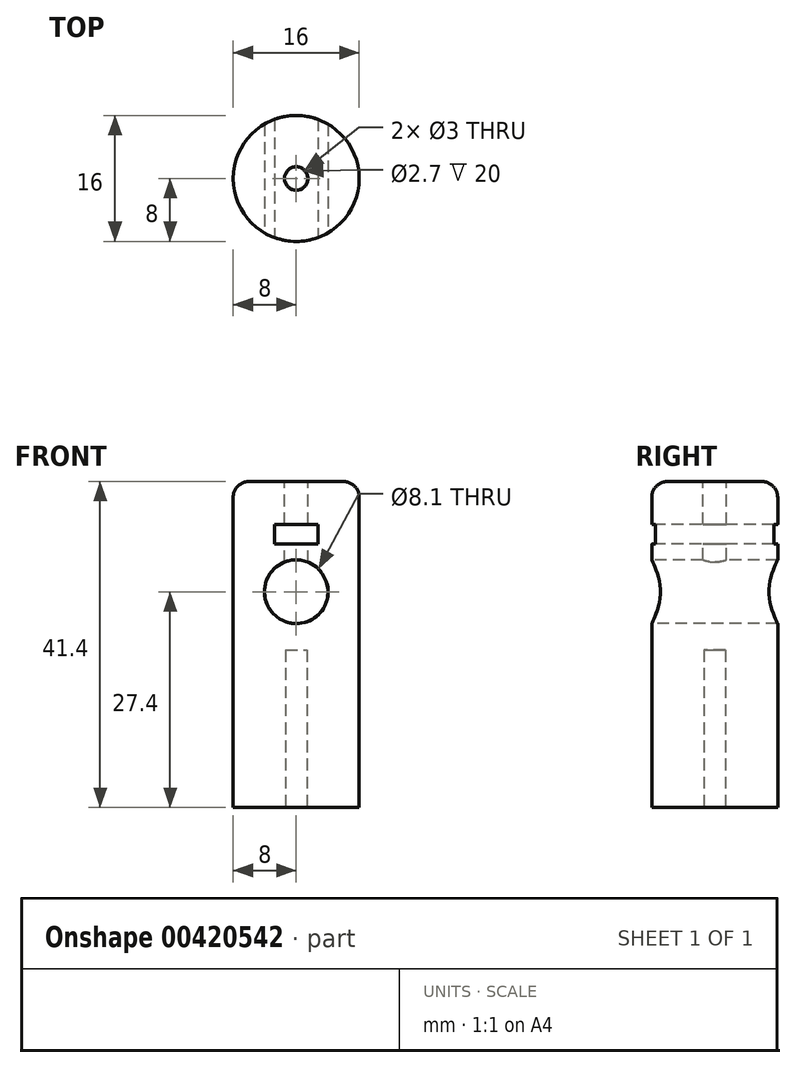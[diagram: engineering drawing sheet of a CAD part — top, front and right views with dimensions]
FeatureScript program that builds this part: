
annotation { "Feature Type Name" : "Feature", "Feature Type Description" : "" }
export const myFeature = defineFeature(function(context is Context, id is Id, definition is map)
    precondition{}
    {
        {
            var Q0;
            Q0=qCreatedBy(makeId("Top.planeOp"),FACE);
            var sketch = newSketch(context, id + "F0", { "sketchPlane" : qUnion([Q0])});
            skCircle(sketch, "E0", {"center": v(0, 0) * mm, "radius": 8 * mm});
            skSolve(sketch);
        }
        {
            var Q0;
            Q0=makeQuery(id+"F0.imprint","IMPRINT",FACE,{"disambiguationData":[TD([[makeQuery(id+"F0.imprint","IMPRINT",EDGE,{"derivedFrom":sQuery(id+"F0.wireOp",EDGE,"E0")}),1.0]])]});
            extrude(context, id + "F1", {"entities" : qUnion([Q0]), "depth" : (45 - 3.6) * mm});
        }
        {
            var Q0;
            Q0=qCreatedBy(makeId("Front.planeOp"),FACE);
            var sketch = newSketch(context, id + "F2", { "sketchPlane" : qUnion([Q0])});
            skCircle(sketch, "E1", {"center": v(0, 27.4) * mm, "radius": 4.05 * mm});
            skLineSegment(sketch, "E2.bottom", {"start": v(2.75, 33.45) * mm, "end": v(-2.75, 33.45) * mm});
            skLineSegment(sketch, "E2.top", {"start": v(2.75, 35.95) * mm, "end": v(-2.75, 35.95) * mm});
            skLineSegment(sketch, "E2.left", {"start": v(2.75, 33.45) * mm, "end": v(2.75, 35.95) * mm});
            skLineSegment(sketch, "E2.right", {"start": v(-2.75, 33.45) * mm, "end": v(-2.75, 35.95) * mm});
            skPoint(sketch, "E2.middle", {"position": v(0, 34.7) * mm});
            skSolve(sketch);
        }
        {
            var Q0;
            Q0=makeQuery(id+"F2.imprint","IMPRINT",FACE,{"disambiguationData":[TD([[makeQuery(id+"F2.imprint","IMPRINT",EDGE,{"derivedFrom":sQuery(id+"F2.wireOp",EDGE,"E1")}),1.0]])]});
            var Q1;
            Q1=makeQuery(id+"F2.imprint","IMPRINT",FACE,{"disambiguationData":[TD([[makeQuery(id+"F2.imprint","IMPRINT",EDGE,{"derivedFrom":sQuery(id+"F2.wireOp",EDGE,"E2.bottom")}),-1.0]])]});
            extrude(context, id + "F3", {"entities" : qUnion([Q0, Q1]), "operationType" : NewBodyOperationType.REMOVE, "endBound" : BoundingType.SYMMETRIC, "oppositeDirection" : true, "depth" : 25 * mm});
        }
        {
            var Q0;
            Q0=makeQuery(id+"F1.opExtrude","CAP_FACE",FACE,{"disambiguationData":[OSD([sQuery(id+"F0.wireOp",EDGE,"E0")])],"isStart":false});
            var sketch = newSketch(context, id + "F4", { "sketchPlane" : qUnion([Q0])});
            skCircle(sketch, "E3", {"center": v(0, 0) * mm, "radius": 1.5 * mm});
            skSolve(sketch);
        }
        {
            var Q0;
            Q0=makeQuery(id+"F4.imprint","IMPRINT",FACE,{"disambiguationData":[TD([[makeQuery(id+"F4.imprint","IMPRINT",EDGE,{"derivedFrom":sQuery(id+"F4.wireOp",EDGE,"E3")}),1.0]])]});
            extrude(context, id + "F5", {"entities" : qUnion([Q0]), "operationType" : NewBodyOperationType.REMOVE, "oppositeDirection" : true, "depth" : 16 * mm});
        }
        {
            var Q0;
            Q0=makeQuery(id+"F1.opExtrude","CAP_FACE",FACE,{"disambiguationData":[OSD([sQuery(id+"F0.wireOp",EDGE,"E0")])],"isStart":true});
            var sketch = newSketch(context, id + "F6", { "sketchPlane" : qUnion([Q0])});
            skCircle(sketch, "E4", {"center": v(0, 0) * mm, "radius": 1.35 * mm});
            skSolve(sketch);
        }
        {
            var Q0;
            Q0 = qSketchRegion(id + "F6", true);
            extrude(context, id + "F7", {"entities" : qUnion([Q0]), "operationType" : NewBodyOperationType.REMOVE, "oppositeDirection" : true, "depth" : 20 * mm});
        }
        {
            var Q0;
            Q0=makeQuery(id+"F1.opExtrude","CAP_EDGE",EDGE,{"disambiguationData":[OSD([sQuery(id+"F0.wireOp",EDGE,"E0")])],"isStart":false});
            fillet(context, id + "F8", {"entities" : qUnion([Q0]), "radius" : 2 * mm, "tangentPropagation" : true, "allowEdgeOverflow" : false});
        }
    });
